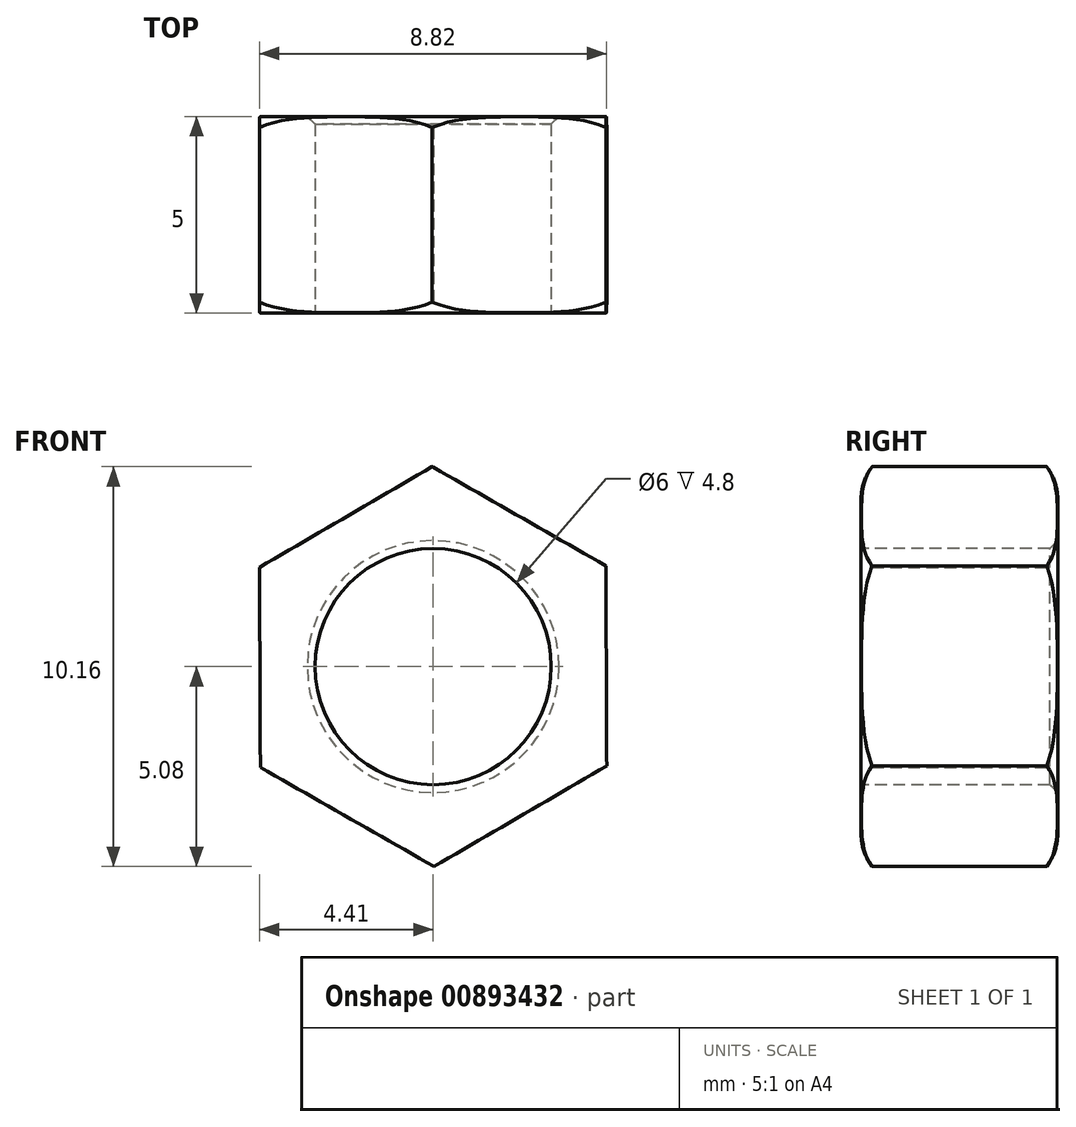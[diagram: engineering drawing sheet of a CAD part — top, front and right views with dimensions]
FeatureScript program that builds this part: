
annotation { "Feature Type Name" : "Feature", "Feature Type Description" : "" }
export const myFeature = defineFeature(function(context is Context, id is Id, definition is map)
    precondition{}
    {
        {
            var Q0;
            Q0=qCreatedBy(makeId("Front.planeOp"),FACE);
            var sketch = newSketch(context, id + "F0", { "sketchPlane" : qUnion([Q0])});
            skCircle(sketch, "E0.cCircle", {"center": v(0, 0) * mm, "radius": 4.4 * mm, "construction": true});
            skLineSegment(sketch, "E0.0", {"start": v(0.02, -5.08) * mm, "end": v(-4.39, -2.56) * mm});
            skLineSegment(sketch, "E0.1", {"start": v(-4.39, -2.56) * mm, "end": v(-4.41, 2.52) * mm});
            skLineSegment(sketch, "E0.2", {"start": v(-4.41, 2.52) * mm, "end": v(-0.02, 5.08) * mm});
            skLineSegment(sketch, "E0.3", {"start": v(-0.02, 5.08) * mm, "end": v(4.39, 2.56) * mm});
            skLineSegment(sketch, "E0.4", {"start": v(4.39, 2.56) * mm, "end": v(4.41, -2.52) * mm});
            skLineSegment(sketch, "E0.5", {"start": v(4.41, -2.52) * mm, "end": v(0.02, -5.08) * mm});
            skPoint(sketch, "E0.0.midPoint", {"position": v(-2.18, -3.82) * mm});
            skSolve(sketch);
        }
        {
            var Q0;
            Q0=makeQuery(id+"F0.imprint","IMPRINT",FACE,{"disambiguationData":[TD([[makeQuery(id+"F0.imprint","IMPRINT",EDGE,{"derivedFrom":sQuery(id+"F0.wireOp",EDGE,"E0.0")}),-1.0]])]});
            extrude(context, id + "F1", {"entities" : qUnion([Q0]), "depth" : 5 * mm, "offsetDistance" : 25 * mm});
        }
        {
            var Q0;
            Q0=makeQuery(id+"F1.opExtrude","CAP_FACE",FACE,{"disambiguationData":[OSD([sQuery(id+"F0.wireOp",EDGE,"E0.0"),sQuery(id+"F0.wireOp",EDGE,"E0.1"),sQuery(id+"F0.wireOp",EDGE,"E0.2"),sQuery(id+"F0.wireOp",EDGE,"E0.3"),sQuery(id+"F0.wireOp",EDGE,"E0.4"),sQuery(id+"F0.wireOp",EDGE,"E0.5")])],"isStart":false});
            var sketch = newSketch(context, id + "F2", { "sketchPlane" : qUnion([Q0])});
            skCircle(sketch, "E1", {"center": v(0, 0) * mm, "radius": 3 * mm});
            skSolve(sketch);
        }
        {
            var Q0;
            Q0=makeQuery(id+"F2.imprint","IMPRINT",FACE,{"disambiguationData":[TD([[makeQuery(id+"F2.imprint","IMPRINT",EDGE,{"derivedFrom":sQuery(id+"F2.wireOp",EDGE,"E1")}),1.0]])]});
            extrude(context, id + "F3", {"entities" : qUnion([Q0]), "operationType" : NewBodyOperationType.REMOVE, "oppositeDirection" : true, "depth" : 25 * mm, "offsetDistance" : 25 * mm});
        }
        {
            var Q0;
            Q0=makeQuery(id+"F3.boolean.opBoolean","COPY",EDGE,{"derivedFrom":makeQuery(id+"F3.opExtrude","CAP_EDGE",EDGE,{"disambiguationData":[OSD([sQuery(id+"F2.wireOp",EDGE,"E1")])],"isStart":true})});
            var Q1;
            Q1=makeQuery(id+"F3.boolean.opBoolean","INTERSECT",EDGE,{"derivedFrom":[makeQuery(id+"F1.opExtrude","CAP_FACE",FACE,{"disambiguationData":[OSD([sQuery(id+"F0.wireOp",EDGE,"E0.0"),sQuery(id+"F0.wireOp",EDGE,"E0.1"),sQuery(id+"F0.wireOp",EDGE,"E0.2"),sQuery(id+"F0.wireOp",EDGE,"E0.3"),sQuery(id+"F0.wireOp",EDGE,"E0.4"),sQuery(id+"F0.wireOp",EDGE,"E0.5")])],"isStart":true}),makeQuery(id+"F3.opExtrude","SWEPT_FACE",FACE,{"disambiguationData":[OSD([sQuery(id+"F2.wireOp",EDGE,"E1")])]})]});
            chamfer(context, id + "F4", {"entities" : qUnion([Q0, Q1]), "width" : 0.2 * mm, "tangentPropagation" : true});
        }
        {
            var Q0;
            Q0=qCreatedBy(makeId("Top.planeOp"),FACE);
            var sketch = newSketch(context, id + "F5", { "sketchPlane" : qUnion([Q0])});
            skLineSegment(sketch, "E2", {"start": v(0, -5) * mm, "end": v(-4.24, -5) * mm});
            skLineSegment(sketch, "E3", {"start": v(-5.38, -4.4) * mm, "end": v(-5.38, -6.96) * mm});
            skLineSegment(sketch, "E4", {"start": v(-5.38, -6.96) * mm, "end": v(0, -6.96) * mm});
            skLineSegment(sketch, "E5", {"start": v(0, -6.96) * mm, "end": v(0, -5) * mm});
            skArc(sketch, "E6", {"start": v(-5.38, -4.4) * mm, "mid": v(-4.88, -4.84) * mm, "end": v(-4.24, -5) * mm});
            skLineSegment(sketch, "E7.MirrorCS", {"start": v(-5.38, 1.96) * mm, "end": v(0, 1.96) * mm});
            skLineSegment(sketch, "E8.MirrorCS", {"start": v(0, 1.96) * mm, "end": v(0, 0) * mm});
            skLineSegment(sketch, "E9.MirrorCS", {"start": v(-5.38, -0.6) * mm, "end": v(-5.38, 1.96) * mm});
            skLineSegment(sketch, "E10.MirrorCS", {"start": v(0, 0) * mm, "end": v(-4.24, 0) * mm});
            skArc(sketch, "E11.MirrorCS", {"start": v(-5.38, -0.6) * mm, "mid": v(-4.88, -0.16) * mm, "end": v(-4.24, 0) * mm});
            skSolve(sketch);
        }
        {
            var Q0;
            Q0=makeQuery(id+"F5.imprint","IMPRINT",FACE,{"disambiguationData":[TD([[makeQuery(id+"F5.imprint","IMPRINT",EDGE,{"derivedFrom":sQuery(id+"F5.wireOp",EDGE,"E2")}),1.0]])]});
            var Q1;
            Q1=makeQuery(id+"F5.imprint","IMPRINT",FACE,{"disambiguationData":[TD([[makeQuery(id+"F5.imprint","IMPRINT",EDGE,{"derivedFrom":sQuery(id+"F5.wireOp",EDGE,"E7.MirrorCS")}),-1.0]])]});
            var Q2;
            Q2=makeQuery(id+"F3.boolean.opBoolean","COPY",FACE,{"derivedFrom":makeQuery(id+"F3.opExtrude","SWEPT_FACE",FACE,{"disambiguationData":[OSD([sQuery(id+"F2.wireOp",EDGE,"E1")])]})});
            revolve(context, id + "F6", {"operationType" : NewBodyOperationType.REMOVE, "surfaceOperationType" : NewSurfaceOperationType.NEW, "entities" : qUnion([Q0, Q1]), "axis" : qUnion([Q2]), "revolveType" : RevolveType.FULL, "oppositeDirection" : true});
        }
    });
